# Revit family: QF_Kelvinator_738341_KCHRI27R1DFE-220_1-Door_220V_Full_Height_Freezer_27_Long
name_source: partatom
category: Specialty Equipment
units: mm (PartAtom-declared; Revit-internal decimal feet)

## family parameters
Always vertical = Yes
Cut with Voids When Loaded = No
Part Type = Normal
Room Calculation Point = No
Round Connector Dimension = Use Diameter
Shared = No
Work Plane-Based = No

## types (1)
- QF_Kelvinator_738341_KCHRI27R1DFE-220_1-Door_220V_Full_Height_Freezer_27_Long
    Apparent Power = 0 VA
    Conn Conduit = Yes
    Cycle = 50 Hz
    Default Elevation = 0"
    Depth = 32 11/16"
    Description = 1-Door Full Height 220V Freezer 27" Long
    Elec Conn Connection Height = 0"
    Elec Conn RI Height = 0"
    FL Amps = 5 A
    Foodservice Equipment Identifier = Yes
    HP = 4/5
    Height = 83"
    Identify Quantity as Lot = Yes
    Item Number = 738341
    Length = 26 3/4"
    Manufacturer = Kelvinator Commercial
    Max Overcurrent Protection = 0 A
    Min Ckt Ampacity = 0 A
    Model = 738341 (KCHRI27R1DFE-220)
    Number of Poles = 1
    Phase = 1
    Refrigerant Type = R290
    Volts = 220 V
    Watts = 1078 W
    Weight in Pounds = 328.489

## geometry (parser evidence)
native form markers: Sweep x8
no freeform markers — native parametric forms only
